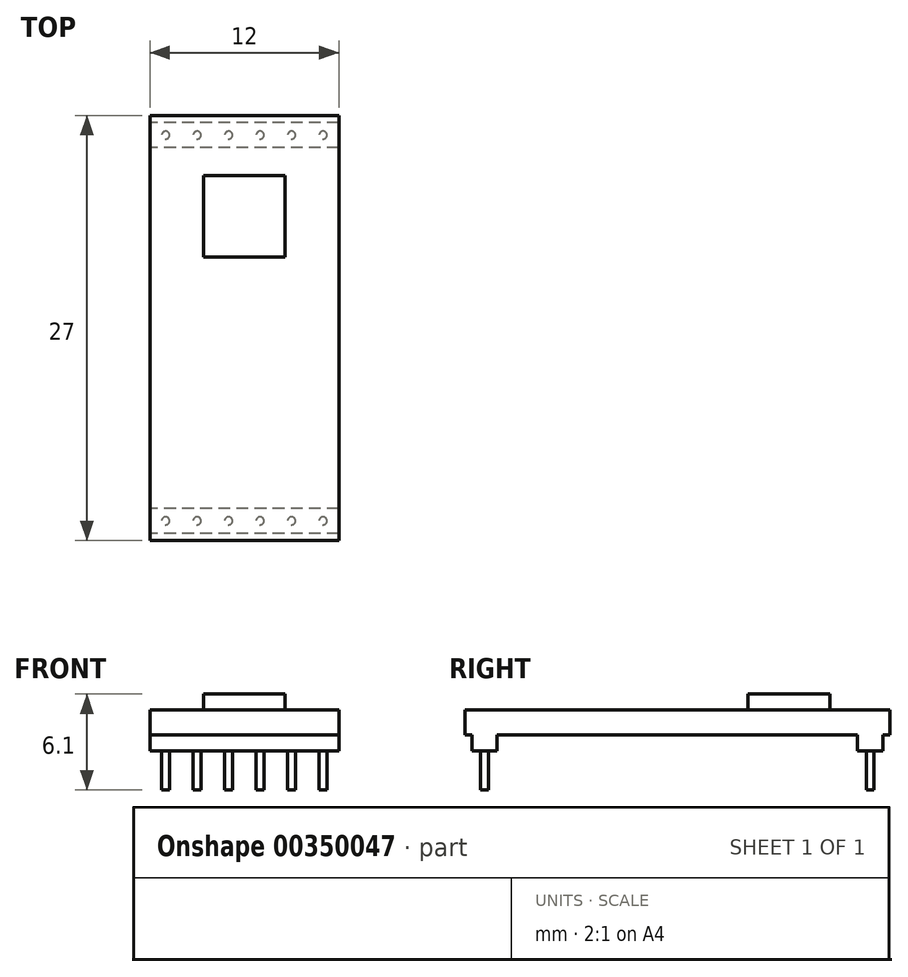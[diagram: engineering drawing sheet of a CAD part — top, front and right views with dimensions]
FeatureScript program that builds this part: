
annotation { "Feature Type Name" : "Feature", "Feature Type Description" : "" }
export const myFeature = defineFeature(function(context is Context, id is Id, definition is map)
    precondition{}
    {
        {
            var Q0;
            Q0=qCreatedBy(makeId("Top.planeOp"),FACE);
            var sketch = newSketch(context, id + "F0", { "sketchPlane" : qUnion([Q0])});
            skLineSegment(sketch, "E0.bottom", {"start": v(-6, 13.5) * mm, "end": v(6, 13.5) * mm});
            skLineSegment(sketch, "E0.top", {"start": v(-6, -13.5) * mm, "end": v(6, -13.5) * mm});
            skLineSegment(sketch, "E0.left", {"start": v(-6, 13.5) * mm, "end": v(-6, -13.5) * mm});
            skLineSegment(sketch, "E0.right", {"start": v(6, 13.5) * mm, "end": v(6, -13.5) * mm});
            skPoint(sketch, "E0.middle", {"position": v(0, 0) * mm});
            skSolve(sketch);
        }
        {
            var Q0;
            Q0=qSketchRegion(id+"F0",true);
            extrude(context, id + "F1", {"entities" : qUnion([Q0]), "depth" : 1.6 * mm});
        }
        {
            var Q0;
            Q0=makeQuery(id+"F1.opExtrude","CAP_FACE",FACE,{"disambiguationData":[OSD([sQuery(id+"F0.wireOp",EDGE,"E0.bottom"),sQuery(id+"F0.wireOp",EDGE,"E0.top"),sQuery(id+"F0.wireOp",EDGE,"E0.left"),sQuery(id+"F0.wireOp",EDGE,"E0.right")])],"isStart":true});
            var sketch = newSketch(context, id + "F2", { "sketchPlane" : qUnion([Q0])});
            skLineSegment(sketch, "E1.bottom", {"start": v(6, -13.05) * mm, "end": v(-6, -13.05) * mm});
            skLineSegment(sketch, "E1.top", {"start": v(6, -11.45) * mm, "end": v(-6, -11.45) * mm});
            skLineSegment(sketch, "E1.left", {"start": v(6, -13.05) * mm, "end": v(6, -11.45) * mm});
            skLineSegment(sketch, "E1.right", {"start": v(-6, -13.05) * mm, "end": v(-6, -11.45) * mm});
            skPoint(sketch, "E1.middle", {"position": v(0, -12.25) * mm});
            skLineSegment(sketch, "E2.bottom", {"start": v(6, 11.45) * mm, "end": v(-6, 11.45) * mm});
            skLineSegment(sketch, "E2.top", {"start": v(6, 13.05) * mm, "end": v(-6, 13.05) * mm});
            skLineSegment(sketch, "E2.left", {"start": v(6, 11.45) * mm, "end": v(6, 13.05) * mm});
            skLineSegment(sketch, "E2.right", {"start": v(-6, 11.45) * mm, "end": v(-6, 13.05) * mm});
            skPoint(sketch, "E2.middle", {"position": v(0, 12.25) * mm});
            skSolve(sketch);
        }
        {
            var Q0;
            Q0=qSketchRegion(id+"F2",true);
            extrude(context, id + "F3", {"entities" : qUnion([Q0]), "operationType" : NewBodyOperationType.ADD, "depth" : 1 * mm});
        }
        {
            var Q0;
            Q0=makeQuery(id+"F3.opExtrude","CAP_FACE",FACE,{"disambiguationData":[OSD([sQuery(id+"F2.wireOp",EDGE,"E1.bottom"),sQuery(id+"F2.wireOp",EDGE,"E1.top"),sQuery(id+"F2.wireOp",EDGE,"E1.left"),sQuery(id+"F2.wireOp",EDGE,"E1.right")])],"isStart":false});
            var sketch = newSketch(context, id + "F4", { "sketchPlane" : qUnion([Q0])});
            skCircle(sketch, "E3", {"center": v(-5, -12.25) * mm, "radius": 0.25 * mm});
            skCircle(sketch, "E4.0.1.0", {"center": v(-5, 12.25) * mm, "radius": 0.25 * mm});
            skCircle(sketch, "E4.1.0.0", {"center": v(-3, -12.25) * mm, "radius": 0.25 * mm});
            skCircle(sketch, "E4.1.1.0", {"center": v(-3, 12.25) * mm, "radius": 0.25 * mm});
            skCircle(sketch, "E4.2.0.0", {"center": v(-1, -12.25) * mm, "radius": 0.25 * mm});
            skCircle(sketch, "E4.2.1.0", {"center": v(-1, 12.25) * mm, "radius": 0.25 * mm});
            skCircle(sketch, "E4.3.0.0", {"center": v(1, -12.25) * mm, "radius": 0.25 * mm});
            skCircle(sketch, "E4.3.1.0", {"center": v(1, 12.25) * mm, "radius": 0.25 * mm});
            skCircle(sketch, "E4.4.0.0", {"center": v(3, -12.25) * mm, "radius": 0.25 * mm});
            skCircle(sketch, "E4.4.1.0", {"center": v(3, 12.25) * mm, "radius": 0.25 * mm});
            skCircle(sketch, "E4.5.0.0", {"center": v(5, -12.25) * mm, "radius": 0.25 * mm});
            skCircle(sketch, "E4.5.1.0", {"center": v(5, 12.25) * mm, "radius": 0.25 * mm});
            skLineSegment(sketch, "E4.direction1", {"start": v(-5, -12.25) * mm, "end": v(-3, -12.25) * mm, "construction": true});
            skLineSegment(sketch, "E4.direction2", {"start": v(-5, -12.25) * mm, "end": v(-5, 12.25) * mm, "construction": true});
            skPoint(sketch, "E5", {"position": v(-6, -12.25) * mm});
            skSolve(sketch);
        }
        {
            var Q0;
            Q0=qSketchRegion(id+"F4",true);
            extrude(context, id + "F5", {"entities" : qUnion([Q0]), "operationType" : NewBodyOperationType.ADD, "depth" : 2.5 * mm});
        }
        {
            var Q0;
            Q0=makeQuery(id+"F1.opExtrude","CAP_FACE",FACE,{"disambiguationData":[OSD([sQuery(id+"F0.wireOp",EDGE,"E0.bottom"),sQuery(id+"F0.wireOp",EDGE,"E0.top"),sQuery(id+"F0.wireOp",EDGE,"E0.left"),sQuery(id+"F0.wireOp",EDGE,"E0.right")])],"isStart":false});
            var sketch = newSketch(context, id + "F6", { "sketchPlane" : qUnion([Q0])});
            skLineSegment(sketch, "E6.bottom", {"start": v(-2.6, 4.5) * mm, "end": v(2.6, 4.5) * mm});
            skLineSegment(sketch, "E6.top", {"start": v(-2.6, 9.68) * mm, "end": v(2.6, 9.68) * mm});
            skLineSegment(sketch, "E6.left", {"start": v(-2.6, 4.5) * mm, "end": v(-2.6, 9.68) * mm});
            skLineSegment(sketch, "E6.right", {"start": v(2.6, 4.5) * mm, "end": v(2.6, 9.68) * mm});
            skPoint(sketch, "E6.middle", {"position": v(0, 7.09) * mm});
            skSolve(sketch);
        }
        {
            var Q0;
            Q0=qSketchRegion(id+"F6",true);
            extrude(context, id + "F7", {"entities" : qUnion([Q0]), "operationType" : NewBodyOperationType.ADD, "depth" : 1 * mm});
        }
    });
